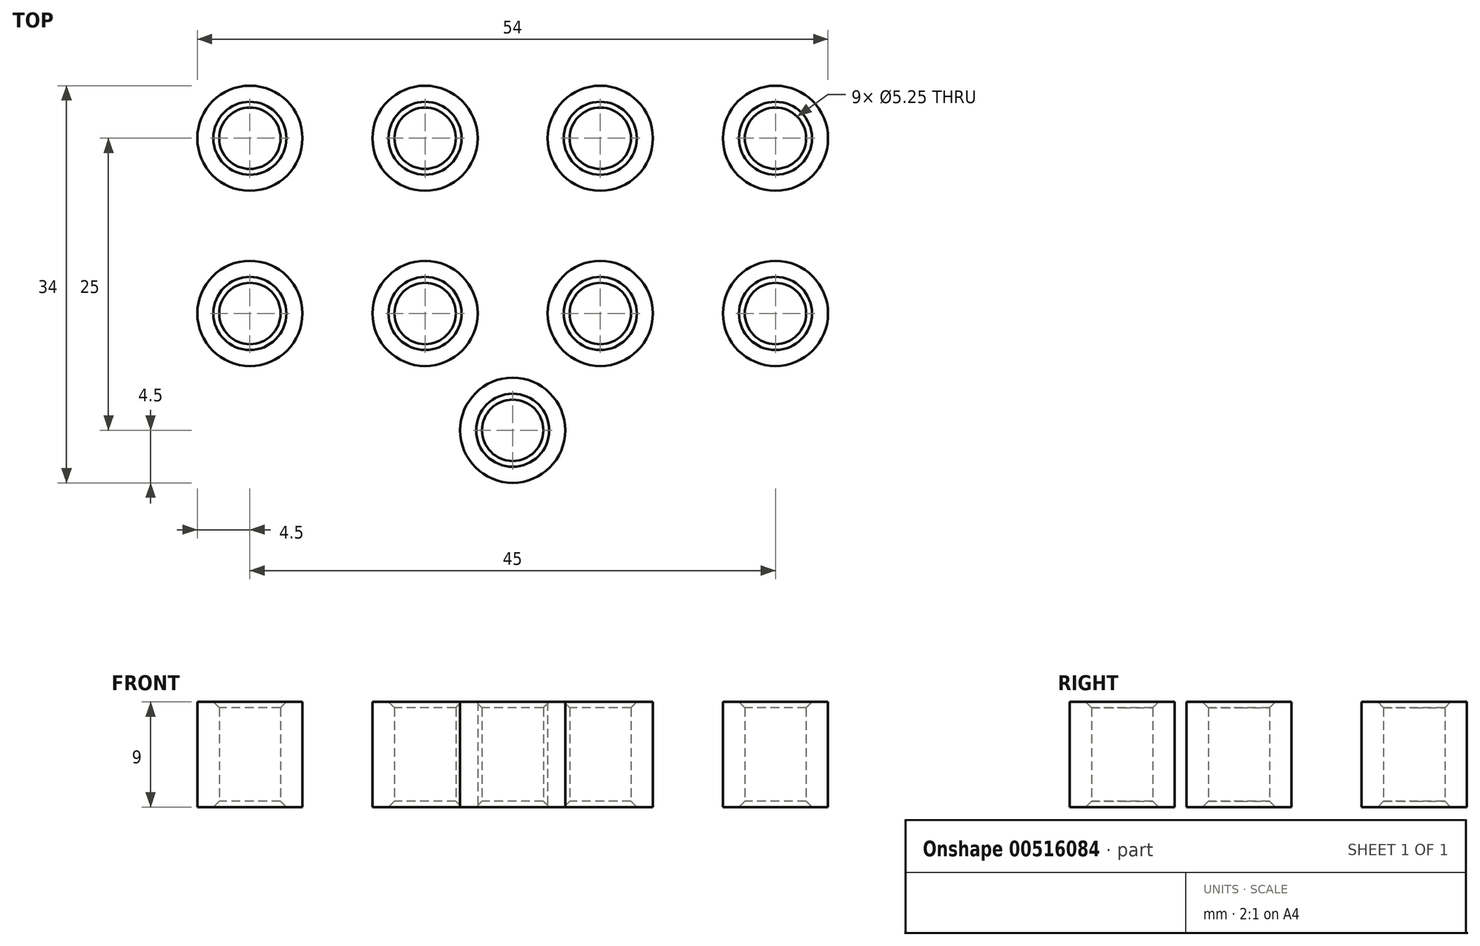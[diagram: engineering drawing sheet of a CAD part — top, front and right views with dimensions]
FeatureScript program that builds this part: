
annotation { "Feature Type Name" : "Feature", "Feature Type Description" : "" }
export const myFeature = defineFeature(function(context is Context, id is Id, definition is map)
    precondition{}
    {
        {
            var Q0;
            Q0=qCreatedBy(makeId("Top.planeOp"),FACE);
            var sketch = newSketch(context, id + "F0", { "sketchPlane" : qUnion([Q0])});
            skCircle(sketch, "E0", {"center": v(-11.34, 6.9) * mm, "radius": 2.62 * mm});
            skCircle(sketch, "E1", {"center": v(-11.34, 6.9) * mm, "radius": 4.5 * mm});
            skSolve(sketch);
        }
        {
            var Q0;
            Q0=makeQuery(id+"F0.imprint","IMPRINT",FACE,{"disambiguationData":[TD([[makeQuery(id+"F0.imprint","IMPRINT",EDGE,{"derivedFrom":sQuery(id+"F0.wireOp",EDGE,"E0")}),-1.0]])]});
            extrude(context, id + "F1", {"entities" : qUnion([Q0]), "depth" : 9 * mm, "offsetDistance" : 25 * mm});
        }
        {
            var Q0;
            Q0=makeQuery(id+"F1.opExtrude","SWEPT_BODY",BODY,{"disambiguationData":[OSD([sQuery(id+"F0.wireOp",EDGE,"E0"),sQuery(id+"F0.wireOp",EDGE,"E1")])]});
            transform(context, id + "F2", {"entities" : qUnion([Q0]), "transformType" : TransformType.TRANSLATION_3D, "dx" : 15 * mm, "dy" : 0 * mm, "dz" : 0 * mm, "makeCopy" : true});
        }
        {
            var Q0;
            Q0=makeQuery(id+"F1.opExtrude","SWEPT_BODY",BODY,{"disambiguationData":[OSD([sQuery(id+"F0.wireOp",EDGE,"E0"),sQuery(id+"F0.wireOp",EDGE,"E1")])]});
            transform(context, id + "F3", {"entities" : qUnion([Q0]), "transformType" : TransformType.TRANSLATION_3D, "dx" : 0 * mm, "dy" : 15 * mm, "dz" : 0 * mm, "makeCopy" : true});
        }
        {
            var Q0;
            Q0=makeQuery(id+"F1.opExtrude","SWEPT_BODY",BODY,{"disambiguationData":[OSD([sQuery(id+"F0.wireOp",EDGE,"E0"),sQuery(id+"F0.wireOp",EDGE,"E1")])]});
            transform(context, id + "F4", {"entities" : qUnion([Q0]), "transformType" : TransformType.TRANSLATION_3D, "dx" : 15 * mm, "dy" : 15 * mm, "dz" : 0 * mm, "makeCopy" : true});
        }
        {
            var Q0;
            Q0=makeQuery(id+"F1.opExtrude","SWEPT_BODY",BODY,{"disambiguationData":[OSD([sQuery(id+"F0.wireOp",EDGE,"E0"),sQuery(id+"F0.wireOp",EDGE,"E1")])]});
            var Q1;
            Q1=makeQuery(id+"F2.opPattern","COPY",BODY,{"derivedFrom":makeQuery(id+"F1.opExtrude","SWEPT_BODY",BODY,{"disambiguationData":[OSD([sQuery(id+"F0.wireOp",EDGE,"E0"),sQuery(id+"F0.wireOp",EDGE,"E1")])]}),"instanceName":"1"});
            var Q2;
            Q2=makeQuery(id+"F3.opPattern","COPY",BODY,{"derivedFrom":makeQuery(id+"F1.opExtrude","SWEPT_BODY",BODY,{"disambiguationData":[OSD([sQuery(id+"F0.wireOp",EDGE,"E0"),sQuery(id+"F0.wireOp",EDGE,"E1")])]}),"instanceName":"1"});
            var Q3;
            Q3=makeQuery(id+"F4.opPattern","COPY",BODY,{"derivedFrom":makeQuery(id+"F1.opExtrude","SWEPT_BODY",BODY,{"disambiguationData":[OSD([sQuery(id+"F0.wireOp",EDGE,"E0"),sQuery(id+"F0.wireOp",EDGE,"E1")])]}),"instanceName":"1"});
            transform(context, id + "F5", {"entities" : qUnion([Q0, Q1, Q2, Q3]), "transformType" : TransformType.TRANSLATION_3D, "dx" : 30 * mm, "dy" : 0 * mm, "dz" : 0 * mm, "makeCopy" : true});
        }
        {
            var Q0;
            Q0=makeQuery(id+"F1.opExtrude","SWEPT_BODY",BODY,{"disambiguationData":[OSD([sQuery(id+"F0.wireOp",EDGE,"E0"),sQuery(id+"F0.wireOp",EDGE,"E1")])]});
            var Q1;
            Q1=makeQuery(id+"F2.opPattern","COPY",BODY,{"derivedFrom":makeQuery(id+"F1.opExtrude","SWEPT_BODY",BODY,{"disambiguationData":[OSD([sQuery(id+"F0.wireOp",EDGE,"E0"),sQuery(id+"F0.wireOp",EDGE,"E1")])]}),"instanceName":"1"});
            var Q2;
            Q2=makeQuery(id+"F5.opPattern","COPY",BODY,{"derivedFrom":makeQuery(id+"F3.opPattern","COPY",BODY,{"derivedFrom":makeQuery(id+"F1.opExtrude","SWEPT_BODY",BODY,{"disambiguationData":[OSD([sQuery(id+"F0.wireOp",EDGE,"E0"),sQuery(id+"F0.wireOp",EDGE,"E1")])]}),"instanceName":"1"}),"instanceName":"1"});
            var Q3;
            Q3=makeQuery(id+"F5.opPattern","COPY",BODY,{"derivedFrom":makeQuery(id+"F4.opPattern","COPY",BODY,{"derivedFrom":makeQuery(id+"F1.opExtrude","SWEPT_BODY",BODY,{"disambiguationData":[OSD([sQuery(id+"F0.wireOp",EDGE,"E0"),sQuery(id+"F0.wireOp",EDGE,"E1")])]}),"instanceName":"1"}),"instanceName":"1"});
            var Q4;
            Q4=makeQuery(id+"F3.opPattern","COPY",BODY,{"derivedFrom":makeQuery(id+"F1.opExtrude","SWEPT_BODY",BODY,{"disambiguationData":[OSD([sQuery(id+"F0.wireOp",EDGE,"E0"),sQuery(id+"F0.wireOp",EDGE,"E1")])]}),"instanceName":"1"});
            var Q5;
            Q5=makeQuery(id+"F5.opPattern","COPY",BODY,{"derivedFrom":makeQuery(id+"F2.opPattern","COPY",BODY,{"derivedFrom":makeQuery(id+"F1.opExtrude","SWEPT_BODY",BODY,{"disambiguationData":[OSD([sQuery(id+"F0.wireOp",EDGE,"E0"),sQuery(id+"F0.wireOp",EDGE,"E1")])]}),"instanceName":"1"}),"instanceName":"1"});
            var Q6;
            Q6=makeQuery(id+"F4.opPattern","COPY",BODY,{"derivedFrom":makeQuery(id+"F1.opExtrude","SWEPT_BODY",BODY,{"disambiguationData":[OSD([sQuery(id+"F0.wireOp",EDGE,"E0"),sQuery(id+"F0.wireOp",EDGE,"E1")])]}),"instanceName":"1"});
            var Q7;
            Q7=makeQuery(id+"F5.opPattern","COPY",BODY,{"derivedFrom":makeQuery(id+"F1.opExtrude","SWEPT_BODY",BODY,{"disambiguationData":[OSD([sQuery(id+"F0.wireOp",EDGE,"E0"),sQuery(id+"F0.wireOp",EDGE,"E1")])]}),"instanceName":"1"});
            transform(context, id + "F6", {"entities" : qUnion([Q0, Q1, Q2, Q3, Q4, Q5, Q6, Q7]), "transformType" : TransformType.TRANSLATION_3D, "dx" : -15 * mm, "dy" : 0 * mm, "dz" : 0 * mm, "makeCopy" : false});
        }
        {
            var Q0;
            Q0=makeQuery(id+"F1.opExtrude","SWEPT_BODY",BODY,{"disambiguationData":[OSD([sQuery(id+"F0.wireOp",EDGE,"E0"),sQuery(id+"F0.wireOp",EDGE,"E1")])]});
            transform(context, id + "F7", {"entities" : qUnion([Q0]), "transformType" : TransformType.TRANSLATION_3D, "dx" : 22.5 * mm, "dy" : -10 * mm, "dz" : 0 * mm, "makeCopy" : true});
        }
        {
            var Q0;
            Q0=makeQuery(id+"F3.opPattern","COPY",EDGE,{"derivedFrom":makeQuery(id+"F1.opExtrude","CAP_EDGE",EDGE,{"disambiguationData":[OSD([sQuery(id+"F0.wireOp",EDGE,"E0")])],"isStart":false}),"instanceName":"1"});
            var Q1;
            Q1=makeQuery(id+"F4.opPattern","COPY",EDGE,{"derivedFrom":makeQuery(id+"F1.opExtrude","CAP_EDGE",EDGE,{"disambiguationData":[OSD([sQuery(id+"F0.wireOp",EDGE,"E0")])],"isStart":false}),"instanceName":"1"});
            var Q2;
            Q2=makeQuery(id+"F5.opPattern","COPY",EDGE,{"derivedFrom":makeQuery(id+"F3.opPattern","COPY",EDGE,{"derivedFrom":makeQuery(id+"F1.opExtrude","CAP_EDGE",EDGE,{"disambiguationData":[OSD([sQuery(id+"F0.wireOp",EDGE,"E0")])],"isStart":false}),"instanceName":"1"}),"instanceName":"1"});
            var Q3;
            Q3=makeQuery(id+"F5.opPattern","COPY",EDGE,{"derivedFrom":makeQuery(id+"F1.opExtrude","CAP_EDGE",EDGE,{"disambiguationData":[OSD([sQuery(id+"F0.wireOp",EDGE,"E0")])],"isStart":false}),"instanceName":"1"});
            var Q4;
            Q4=makeQuery(id+"F5.opPattern","COPY",EDGE,{"derivedFrom":makeQuery(id+"F2.opPattern","COPY",EDGE,{"derivedFrom":makeQuery(id+"F1.opExtrude","CAP_EDGE",EDGE,{"disambiguationData":[OSD([sQuery(id+"F0.wireOp",EDGE,"E0")])],"isStart":false}),"instanceName":"1"}),"instanceName":"1"});
            var Q5;
            Q5=makeQuery(id+"F5.opPattern","COPY",EDGE,{"derivedFrom":makeQuery(id+"F4.opPattern","COPY",EDGE,{"derivedFrom":makeQuery(id+"F1.opExtrude","CAP_EDGE",EDGE,{"disambiguationData":[OSD([sQuery(id+"F0.wireOp",EDGE,"E0")])],"isStart":false}),"instanceName":"1"}),"instanceName":"1"});
            var Q6;
            Q6=makeQuery(id+"F7.opPattern","COPY",EDGE,{"derivedFrom":makeQuery(id+"F1.opExtrude","CAP_EDGE",EDGE,{"disambiguationData":[OSD([sQuery(id+"F0.wireOp",EDGE,"E0")])],"isStart":false}),"instanceName":"1"});
            var Q7;
            Q7=makeQuery(id+"F2.opPattern","COPY",EDGE,{"derivedFrom":makeQuery(id+"F1.opExtrude","CAP_EDGE",EDGE,{"disambiguationData":[OSD([sQuery(id+"F0.wireOp",EDGE,"E0")])],"isStart":false}),"instanceName":"1"});
            var Q8;
            Q8=makeQuery(id+"F1.opExtrude","CAP_EDGE",EDGE,{"disambiguationData":[OSD([sQuery(id+"F0.wireOp",EDGE,"E0")])],"isStart":false});
            var Q9;
            Q9=makeQuery(id+"F1.opExtrude","CAP_EDGE",EDGE,{"disambiguationData":[OSD([sQuery(id+"F0.wireOp",EDGE,"E0")])],"isStart":true});
            var Q10;
            Q10=makeQuery(id+"F7.opPattern","COPY",EDGE,{"derivedFrom":makeQuery(id+"F1.opExtrude","CAP_EDGE",EDGE,{"disambiguationData":[OSD([sQuery(id+"F0.wireOp",EDGE,"E0")])],"isStart":true}),"instanceName":"1"});
            var Q11;
            Q11=makeQuery(id+"F2.opPattern","COPY",EDGE,{"derivedFrom":makeQuery(id+"F1.opExtrude","CAP_EDGE",EDGE,{"disambiguationData":[OSD([sQuery(id+"F0.wireOp",EDGE,"E0")])],"isStart":true}),"instanceName":"1"});
            var Q12;
            Q12=makeQuery(id+"F5.opPattern","COPY",EDGE,{"derivedFrom":makeQuery(id+"F1.opExtrude","CAP_EDGE",EDGE,{"disambiguationData":[OSD([sQuery(id+"F0.wireOp",EDGE,"E0")])],"isStart":true}),"instanceName":"1"});
            var Q13;
            Q13=makeQuery(id+"F5.opPattern","COPY",EDGE,{"derivedFrom":makeQuery(id+"F2.opPattern","COPY",EDGE,{"derivedFrom":makeQuery(id+"F1.opExtrude","CAP_EDGE",EDGE,{"disambiguationData":[OSD([sQuery(id+"F0.wireOp",EDGE,"E0")])],"isStart":true}),"instanceName":"1"}),"instanceName":"1"});
            var Q14;
            Q14=makeQuery(id+"F5.opPattern","COPY",EDGE,{"derivedFrom":makeQuery(id+"F4.opPattern","COPY",EDGE,{"derivedFrom":makeQuery(id+"F1.opExtrude","CAP_EDGE",EDGE,{"disambiguationData":[OSD([sQuery(id+"F0.wireOp",EDGE,"E0")])],"isStart":true}),"instanceName":"1"}),"instanceName":"1"});
            var Q15;
            Q15=makeQuery(id+"F5.opPattern","COPY",EDGE,{"derivedFrom":makeQuery(id+"F3.opPattern","COPY",EDGE,{"derivedFrom":makeQuery(id+"F1.opExtrude","CAP_EDGE",EDGE,{"disambiguationData":[OSD([sQuery(id+"F0.wireOp",EDGE,"E0")])],"isStart":true}),"instanceName":"1"}),"instanceName":"1"});
            var Q16;
            Q16=makeQuery(id+"F4.opPattern","COPY",EDGE,{"derivedFrom":makeQuery(id+"F1.opExtrude","CAP_EDGE",EDGE,{"disambiguationData":[OSD([sQuery(id+"F0.wireOp",EDGE,"E0")])],"isStart":true}),"instanceName":"1"});
            var Q17;
            Q17=makeQuery(id+"F3.opPattern","COPY",EDGE,{"derivedFrom":makeQuery(id+"F1.opExtrude","CAP_EDGE",EDGE,{"disambiguationData":[OSD([sQuery(id+"F0.wireOp",EDGE,"E0")])],"isStart":true}),"instanceName":"1"});
            chamfer(context, id + "F8", {"entities" : qUnion([Q0, Q1, Q2, Q3, Q4, Q5, Q6, Q7, Q8, Q9, Q10, Q11, Q12, Q13, Q14, Q15, Q16, Q17]), "width" : .5 * mm, "tangentPropagation" : true});
        }
    });
